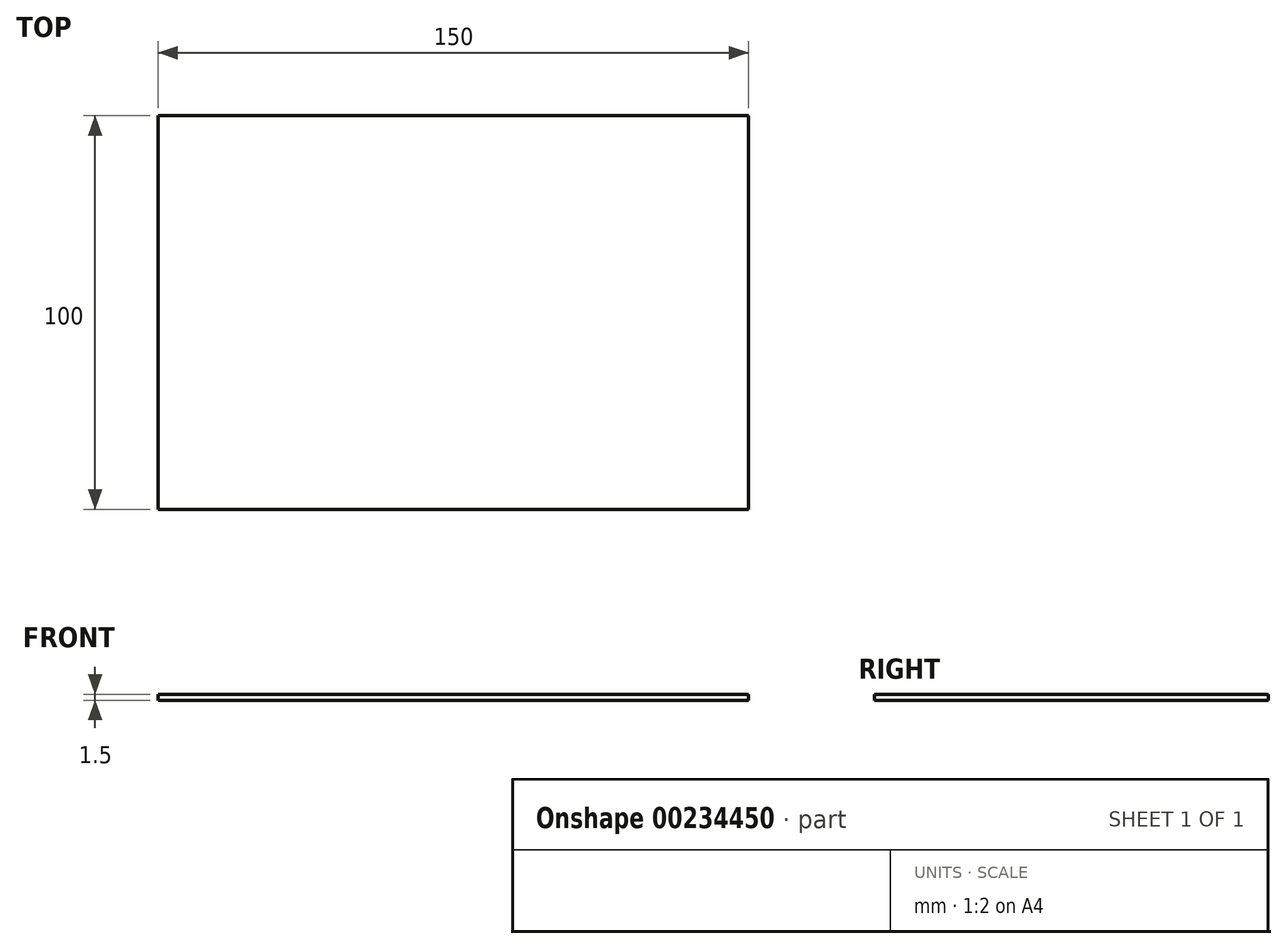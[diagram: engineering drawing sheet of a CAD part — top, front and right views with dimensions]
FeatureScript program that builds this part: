
annotation { "Feature Type Name" : "Feature", "Feature Type Description" : "" }
export const myFeature = defineFeature(function(context is Context, id is Id, definition is map)
    precondition{}
    {
        {
            var Q0;
            Q0=qCreatedBy(makeId("Top.planeOp"),FACE);
            var sketch = newSketch(context, id + "F0", { "sketchPlane" : qUnion([Q0])});
            skLineSegment(sketch, "E0.bottom", {"start": v(-57.9, -52.98) * mm, "end": v(92.1, -52.98) * mm});
            skLineSegment(sketch, "E0.top", {"start": v(-57.9, 47.02) * mm, "end": v(92.1, 47.02) * mm});
            skLineSegment(sketch, "E0.left", {"start": v(-57.9, -52.98) * mm, "end": v(-57.9, 47.02) * mm});
            skLineSegment(sketch, "E0.right", {"start": v(92.1, -52.98) * mm, "end": v(92.1, 47.02) * mm});
            skSolve(sketch);
        }
        {
            var Q0;
            Q0 = qSketchRegion(id + "F0", true);
            extrude(context, id + "F1", {"entities" : qUnion([Q0]), "depth" : 1.5 * mm});
        }
    });
